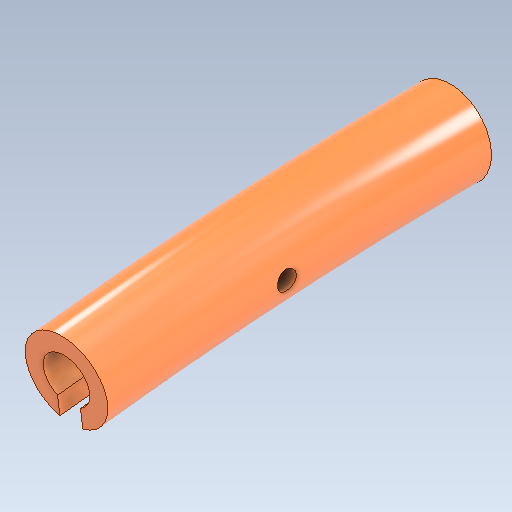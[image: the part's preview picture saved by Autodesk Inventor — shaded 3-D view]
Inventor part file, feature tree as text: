
AUTODESK INVENTOR PART (.ipt)
format: ipt  version: 2021 (Build 250183000, 183)  size: 221,696 bytes
history: native  units: mm
features: sketch x4, extrude x2, revolve x1
ambient origin geometry x8: Origin, YZ Plane, XZ Plane, XY Plane, X Axis, Y Axis, Z Axis, Center Point
bodies: Solid1 (feature_tree)
feature tree (7):
  sketch  "Sketch1"  dims[d0=3300.0mm d1=1650.0mm]
  revolve  "Revolution1"  [1 undecoded]
  extrude  "Extrusion1"  Depth=43.0mm
  extrude  "Extrusion2"  Depth=1.22173mm
  sketch  "Sketch2"  dims[d2=0.0mm d3=43.0mm]
  sketch  "Sketch3"  dims[d4=9.3mm d5=1.22173mm]
  sketch  "Sketch4"  dims[d6=12.0mm d7=0.0mm d8=3300.0mm d9=10.0mm d10=100.0mm d11=0.0mm]
note: 1 required parameter value undecoded (feature->parameter linkage not recoverable at this tier; creation-order binding heuristic only, values carry confidence <= 0.55)
